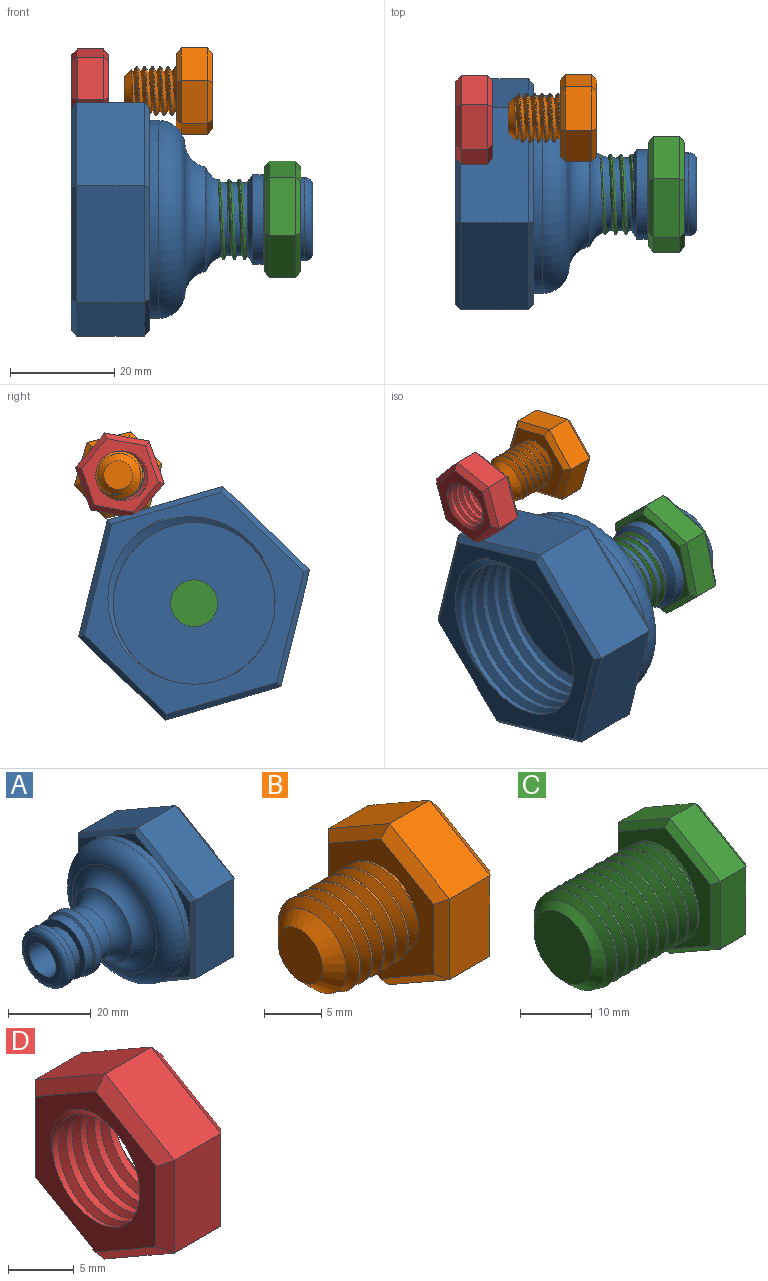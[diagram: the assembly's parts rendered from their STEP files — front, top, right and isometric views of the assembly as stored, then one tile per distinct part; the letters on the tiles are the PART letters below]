
ASSEMBLY  parts=4 mates=2
PART A: 40 faces, bbox 48.4x42.2x47.2 mm
  f0: cylinder r=15.54mm len=31.07mm, axis (1,0,0), area 508.8mm2, adj f8,f21,f22,f23
  f1: plane 19.98x13mm, normal (0,-0.5,0.87), area 300.2mm2, adj f2,f6,f14,f18
  f2: plane 23.09x13mm, normal (0,-1,0), area 300.2mm2, adj f1,f3,f12,f16
  f3: plane 20.02x13mm, normal (0,-0.5,-0.87), area 300.2mm2, adj f2,f4,f10,f15
  f4: plane 19.98x13mm, normal (0,0.5,-0.87), area 300.2mm2, adj f3,f5,f9,f17
  f5: plane 23.09x13mm, normal (0,1,0), area 300.2mm2, adj f4,f6,f11,f19
  f6: plane 20.02x13mm, normal (0,0.5,0.87), area 300.2mm2, adj f1,f5,f13,f20
  f7: plane 43.88x38.04mm, normal (-1,0,0), area 116.4mm2, adj f9,f10,f11,f12,f13,f14,f24
  f8: plane 44.91x39.06mm, normal (1,0,0), area 436.8mm2, adj f0,f15,f16,f17,f18,f19,f20,f21
  f9: plane 19.98x12.15mm, normal (-0.71,0.35,-0.61), area 31.8mm2, adj f4,f7,f10,f11
  f10: plane 20.02x12.09mm, normal (-0.71,-0.35,-0.61), area 31.8mm2, adj f3,f7,f9,f12
  f11: plane 23.09x1.04mm, normal (-0.71,0.71,0), area 31.8mm2, adj f5,f7,f9,f13
  f12: plane 23.09x1.04mm, normal (-0.71,-0.71,0), area 31.8mm2, adj f2,f7,f10,f14
  f13: plane 20.02x12.09mm, normal (-0.71,0.35,0.61), area 31.8mm2, adj f6,f7,f11,f14
  f14: plane 19.98x12.15mm, normal (-0.71,-0.35,0.61), area 31.8mm2, adj f1,f7,f12,f13
  f15: plane 20.02x12.09mm, normal (0.71,-0.35,-0.61), area 31.8mm2, adj f3,f8,f16,f17
  f16: plane 23.09x1.04mm, normal (0.71,-0.71,0), area 31.8mm2, adj f2,f8,f15,f18
  f17: plane 19.98x12.15mm, normal (0.71,0.35,-0.61), area 31.8mm2, adj f4,f8,f15,f19
  f18: plane 19.98x12.15mm, normal (0.71,-0.35,0.61), area 31.8mm2, adj f1,f8,f16,f20
  f19: plane 23.09x1.04mm, normal (0.71,0.71,0), area 31.8mm2, adj f5,f8,f17,f20
  f20: plane 20.02x12.09mm, normal (0.71,0.35,0.61), area 31.8mm2, adj f6,f8,f18,f19
  f21: bspline ~39.78x34.45mm, area 988.8mm2, adj f0,f8,f22,f23
  f22: bspline ~39.78x34.45mm, area 988.2mm2, adj f0,f8,f21,f23
  f23: plane 33.23x33.06mm, normal (1,0,0), area 750.1mm2, adj f0,f21,f22,f37
  f24: cylinder r=19mm len=38mm, axis (-1,0,0), area 214.9mm2, adj f7,f38
  f25: cylinder r=8mm len=16mm, axis (-1,0,0), area 125.7mm2, adj f26,f34
  f26: cone r=8.6mm half-angle=50.2deg, axis (1,0,0), area 40.7mm2, adj f25,f27
  f27: cylinder r=8.6mm len=17.2mm, axis (-1,0,0), area 108.1mm2, adj f26,f28
  f28: cone r=8.6mm half-angle=58deg, axis (-1,0,0), area 92.5mm2, adj f27,f29
  f29: cylinder r=7mm len=14mm, axis (-1,0,0), area 165.6mm2, adj f28,f35
  f30: plane 13x13mm, normal (-1,0,0), area 69.1mm2, adj f36,f37
  f31: cylinder r=8mm len=16mm, axis (-1,0,0), area 75.4mm2, adj f32,f36
  f32: plane 16x16mm, normal (1,0,0), area 88mm2, adj f31,f33
  f33: cylinder r=6mm len=12mm, axis (-1,0,0), area 131.9mm2, adj f32,f34
  f34: plane 16x16mm, normal (-1,0,0), area 88mm2, adj f25,f33
  f35: torus R=11.49mm, axis (1,0,0), area 280mm2, adj f29,f39
  f36: torus R=6.5mm, axis (1,0,0), area 110.4mm2, adj f30,f31
  f37: cylinder r=4.5mm len=31.5mm, axis (-1,0,0), area 890.6mm2, adj f23,f30
  f38: torus R=14mm, axis (-1,0,0), area 807.3mm2, adj f24,f39
  f39: torus R=14.91mm, axis (1,0,0), area 476.4mm2, adj f35,f38
PART B: 25 faces, bbox 17.8x15.9x18.1 mm
  f0: cylinder r=4.75mm len=9.5mm, axis (1,0,0), area 28.1mm2, adj f1,f2,f4,f12
  f1: bspline ~10.97x9.91mm, area 196.7mm2, adj f0,f2,f4,f12
  f2: bspline ~10.97x10.66mm, area 196.6mm2, adj f0,f1,f4,f12
  f3: plane 5.5x5.5mm, normal (-1,0,0), area 23.8mm2, adj f4
  f4: cone r=4.75mm half-angle=45deg, axis (1,0,0), area 47.4mm2, adj f0,f1,f2,f3
  f5: plane 7.48x5mm, normal (0,-0.5,0.86), area 43.3mm2, adj f6,f10,f18,f22
  f6: plane 8.66x5mm, normal (0,-1,0), area 43.3mm2, adj f5,f7,f16,f20
  f7: plane 7.52x5mm, normal (0,-0.5,-0.87), area 43.3mm2, adj f6,f8,f14,f19
  f8: plane 7.48x5mm, normal (0,0.5,-0.86), area 43.3mm2, adj f7,f9,f13,f21
  f9: plane 8.66x5mm, normal (0,1,0), area 43.3mm2, adj f8,f10,f15,f23
  f10: plane 7.52x5mm, normal (0,0.5,0.87), area 43.3mm2, adj f5,f9,f17,f24
  f11: plane 15.01x13.03mm, normal (1,0,0), area 146.4mm2, adj f13,f14,f15,f16,f17,f18
  f12: plane 15.83x13.85mm, normal (-1,0,0), area 89.2mm2, adj f0,f1,f2,f19,f20,f21,f22,f23
  f13: plane 7.49x4.93mm, normal (0.71,0.36,-0.61), area 11.4mm2, adj f8,f11,f14,f15
  f14: plane 7.52x4.88mm, normal (0.71,-0.35,-0.61), area 11.4mm2, adj f7,f11,f13,f16
  f15: plane 8.66x1.03mm, normal (0.71,0.71,0), area 11.4mm2, adj f9,f11,f13,f17
  f16: plane 8.66x1.03mm, normal (0.71,-0.71,0), area 11.4mm2, adj f6,f11,f14,f18
  f17: plane 7.52x4.88mm, normal (0.71,0.35,0.61), area 11.4mm2, adj f10,f11,f15,f18
  f18: plane 7.49x4.93mm, normal (0.71,-0.36,0.61), area 11.4mm2, adj f5,f11,f16,f17
  f19: plane 7.52x4.88mm, normal (-0.71,-0.35,-0.61), area 11.4mm2, adj f7,f12,f20,f21
  f20: plane 8.66x1.03mm, normal (-0.71,-0.71,0), area 11.4mm2, adj f6,f12,f19,f22
  f21: plane 7.49x4.93mm, normal (-0.71,0.36,-0.61), area 11.4mm2, adj f8,f12,f19,f23
  f22: plane 7.49x4.93mm, normal (-0.71,-0.36,0.61), area 11.4mm2, adj f5,f12,f20,f24
  f23: plane 8.66x1.03mm, normal (-0.71,0.71,0), area 11.4mm2, adj f9,f12,f21,f24
  f24: plane 7.52x4.88mm, normal (-0.71,0.35,0.61), area 11.4mm2, adj f10,f12,f22,f23
PART C: 26 faces, bbox 27.7x20x23.1 mm
  f0: cylinder r=7.68mm len=18mm, axis (1,0,0), area 139.1mm2, adj f1,f2,f5,f13
  f1: bspline ~20.88x17.74mm, area 713.8mm2, adj f0,f2,f4,f5,f13
  f2: bspline ~21.88x17.74mm, area 715.1mm2, adj f0,f1,f4,f5,f13
  f3: plane 11.36x11.36mm, normal (-1,0,0), area 101.4mm2, adj f4
  f4: cone r=7.68mm half-angle=45deg, axis (1,0,0), area 63.2mm2, adj f1,f2,f3,f5
  f5: cone r=7.68mm half-angle=45deg, axis (1,0,0), area 13.2mm2, adj f0,f1,f2,f4
  f6: plane 9.98x5.81mm, normal (0,-0.5,0.86), area 57.7mm2, adj f7,f11,f19,f23
  f7: plane 11.55x5mm, normal (0,-1,0), area 57.7mm2, adj f6,f8,f17,f21
  f8: plane 10.02x5.74mm, normal (0,-0.5,-0.87), area 57.7mm2, adj f7,f9,f15,f20
  f9: plane 9.98x5.81mm, normal (0,0.5,-0.86), area 57.7mm2, adj f8,f10,f14,f22
  f10: plane 11.55x5mm, normal (0,1,0), area 57.7mm2, adj f9,f11,f16,f24
  f11: plane 10.02x5.74mm, normal (0,0.5,0.87), area 57.7mm2, adj f6,f10,f18,f25
  f12: plane 20.78x18.04mm, normal (1,0,0), area 280.6mm2, adj f14,f15,f16,f17,f18,f19
  f13: plane 20.78x18.04mm, normal (-1,0,0), area 125.2mm2, adj f0,f1,f2,f20,f21,f22,f23,f24
  f14: plane 9.98x6.38mm, normal (0.71,0.36,-0.61), area 15.5mm2, adj f9,f12,f15,f16
  f15: plane 10.02x6.32mm, normal (0.71,-0.35,-0.61), area 15.5mm2, adj f8,f12,f14,f17
  f16: plane 11.55x1.04mm, normal (0.71,0.71,0), area 15.5mm2, adj f10,f12,f14,f18
  f17: plane 11.55x1.04mm, normal (0.71,-0.71,0), area 15.5mm2, adj f7,f12,f15,f19
  f18: plane 10.02x6.32mm, normal (0.71,0.35,0.61), area 15.5mm2, adj f11,f12,f16,f19
  f19: plane 9.98x6.38mm, normal (0.71,-0.36,0.61), area 15.5mm2, adj f6,f12,f17,f18
  f20: plane 10.02x6.32mm, normal (-0.71,-0.35,-0.61), area 15.5mm2, adj f8,f13,f21,f22
  f21: plane 11.55x1.04mm, normal (-0.71,-0.71,0), area 15.5mm2, adj f7,f13,f20,f23
  f22: plane 9.98x6.38mm, normal (-0.71,0.36,-0.61), area 15.5mm2, adj f9,f13,f20,f24
  f23: plane 9.98x6.38mm, normal (-0.71,-0.36,0.61), area 15.5mm2, adj f6,f13,f21,f25
  f24: plane 11.55x1.04mm, normal (-0.71,0.71,0), area 15.5mm2, adj f10,f13,f22,f25
  f25: plane 10.02x6.32mm, normal (-0.71,0.35,0.61), area 15.5mm2, adj f11,f13,f23,f24
PART D: 23 faces, bbox 9.1x15.4x17.7 mm
  f0: plane 7.49x5mm, normal (0,-0.5,0.86), area 43.3mm2, adj f1,f5,f13,f17
  f1: plane 8.66x5mm, normal (0,-1,0), area 43.3mm2, adj f0,f2,f11,f15
  f2: plane 7.51x5mm, normal (0,-0.5,-0.87), area 43.3mm2, adj f1,f3,f9,f14
  f3: plane 7.49x5mm, normal (0,0.5,-0.86), area 43.3mm2, adj f2,f4,f8,f16
  f4: plane 8.66x5mm, normal (0,1,0), area 43.3mm2, adj f3,f5,f10,f18
  f5: plane 7.51x5mm, normal (0,0.5,0.87), area 43.3mm2, adj f0,f4,f12,f19
  f6: plane 15.37x13.38mm, normal (-1,0,0), area 71.4mm2, adj f8,f9,f10,f11,f12,f13,f20,f21
  f7: plane 15.37x13.38mm, normal (1,0,0), area 71.4mm2, adj f14,f15,f16,f17,f18,f19,f20,f21
  f8: plane 7.49x4.93mm, normal (-0.71,0.36,-0.61), area 11.4mm2, adj f3,f6,f9,f10
  f9: plane 7.51x4.89mm, normal (-0.71,-0.35,-0.61), area 11.4mm2, adj f2,f6,f8,f11
  f10: plane 8.66x1.02mm, normal (-0.71,0.71,0), area 11.4mm2, adj f4,f6,f8,f12
  f11: plane 8.66x1.02mm, normal (-0.71,-0.71,0), area 11.4mm2, adj f1,f6,f9,f13
  f12: plane 7.51x4.89mm, normal (-0.71,0.35,0.61), area 11.4mm2, adj f5,f6,f10,f13
  f13: plane 7.49x4.93mm, normal (-0.71,-0.36,0.61), area 11.4mm2, adj f0,f6,f11,f12
  f14: plane 7.51x4.89mm, normal (0.71,-0.35,-0.61), area 11.4mm2, adj f2,f7,f15,f16
  f15: plane 8.66x1.02mm, normal (0.71,-0.71,0), area 11.4mm2, adj f1,f7,f14,f17
  f16: plane 7.49x4.93mm, normal (0.71,0.36,-0.61), area 11.4mm2, adj f3,f7,f14,f18
  f17: plane 7.49x4.93mm, normal (0.71,-0.36,0.61), area 11.4mm2, adj f0,f7,f15,f19
  f18: plane 8.66x1.02mm, normal (0.71,0.71,0), area 11.4mm2, adj f4,f7,f16,f19
  f19: plane 7.51x4.89mm, normal (0.71,0.35,0.61), area 11.4mm2, adj f5,f7,f17,f18
  f20: cylinder r=4.66mm len=9.32mm, axis (1,0,0), area 85.4mm2, adj f6,f7,f21,f22
  f21: bspline ~12.5x10.82mm, area 128.4mm2, adj f6,f7,f20,f22
  f22: bspline ~12.5x10.82mm, area 128.5mm2, adj f6,f7,f20,f21
PLACE A rot(axis=(0,0.6,-0.8),180deg) t=(-55.27,-6.86,23.48)mm fixed
PLACE B rot(axis=(-1,0,0),43.8deg) t=(-31.66,7.73,48.08)mm
PLACE C rot(axis=(-1,0,0),134.9deg) t=(-14.77,-6.86,23.48)mm
PLACE D rot(axis=(1,0,0),100.2deg) t=(-48.16,7.38,48.02)mm fixed
MATE cylindrical C.f0 <-> A.f37  axis (-1,0,0) through (-38.27,-6.86,23.48)mm
MATE cylindrical B.f0 <-> D.f6  axis (-1,0,0) through (-45.16,7.73,48.08)mm
